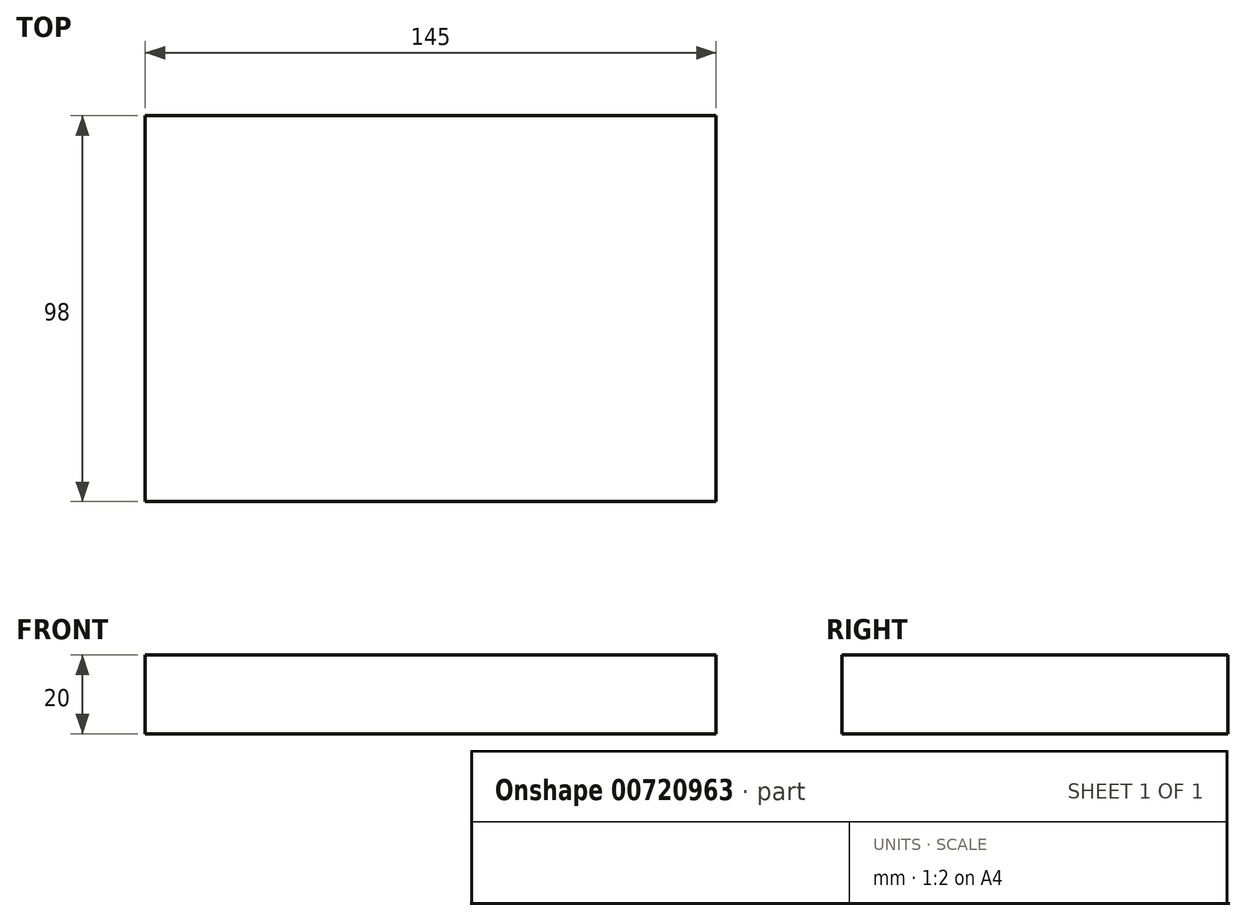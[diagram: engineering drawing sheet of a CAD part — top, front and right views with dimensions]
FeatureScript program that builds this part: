
annotation { "Feature Type Name" : "Feature", "Feature Type Description" : "" }
export const myFeature = defineFeature(function(context is Context, id is Id, definition is map)
    precondition{}
    {
        {
            var Q0;
            Q0=qCreatedBy(makeId("Front.planeOp"),FACE);
            var sketch = newSketch(context, id + "F0", { "sketchPlane" : qUnion([Q0])});
            skLineSegment(sketch, "E0.bottom", {"start": v(72.5, 10) * mm, "end": v(-72.5, 10) * mm});
            skLineSegment(sketch, "E0.top", {"start": v(72.5, -10) * mm, "end": v(-72.5, -10) * mm});
            skLineSegment(sketch, "E0.left", {"start": v(72.5, 10) * mm, "end": v(72.5, -10) * mm});
            skLineSegment(sketch, "E0.right", {"start": v(-72.5, 10) * mm, "end": v(-72.5, -10) * mm});
            skPoint(sketch, "E0.middle", {"position": v(0, 0) * mm});
            skSolve(sketch);
        }
        {
            var Q0;
            Q0 = qSketchRegion(id + "F0", true);
            extrude(context, id + "F1", {"entities" : qUnion([Q0]), "endBound" : BoundingType.SYMMETRIC, "depth" : 98 * mm, "offsetDistance" : 25 * mm});
        }
    });
